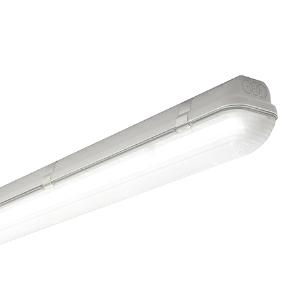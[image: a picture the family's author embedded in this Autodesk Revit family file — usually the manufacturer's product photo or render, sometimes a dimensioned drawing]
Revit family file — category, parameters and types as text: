
# Revit family: 3f_filippi_-_3f_linda_soft_3f_filippi_-_58731_-_3f_linda_led_soft_1x12w_l660
name_source: partatom
category: Lighting Fixtures
units: mm (PartAtom-declared; Revit-internal decimal feet)

## family parameters
Cut with Voids When Loaded = No
Host = Face
Light Source = No
Part Type = Normal
Room Calculation Point = No
Round Connector Dimension = Use Diameter
Shared = No

## types (1)
- 3F Filippi - 3F Linda Soft (1 x LED, 1866 lm, 14 W, 4000 K)
    Apparent Load = 14 VA
    Approval mark = CE
    CIE Flux Codes = 39 68 88 89 100
    Color Rendering = 80
    Color Temperature = 4000 K
    Control Gear = Electronic ballast
    Default Elevation = 1800 mm
    Description = ILLUMINOTECHNICAL
Luminous efficiency 100% (DLOR 89%, ULOR 11%).
Initial luminous flux of the luminaire 1866 lm.
Direct symmetric distribution.
Installation Interdistance Transv.D = 1.39 x hu - Long.D = 1.21 x hu.
Tabular UGR (CIE 117 - 4H-8H; S=0.25H; 70/50/20): RUG 23.7 - 20.5.
Beam angle: 149° - 108°.
Luminous efficacy 133 lm/W.
Lifetime (L93/B10): 30000 h. (tq+25°C)
Lifetime (L90/B10): 50000 h. (tq+25°C)
Lifetime (L85/B10): 80000 h. (tq+25°C)
Lifetime (L80/B10): 100000 h. (tq+25°C)
Lifetime (L85/B10): 50000 h. (tq+35°C)
Sudden decreased luminous flux after 50000 hours: 0% (C0).
Photobiological safety in compliance with IEC/TR 62778: RG0 risk exempt, (IEC 62471).
In compliance with IEC/EN 62722-2-1 - IEC/EN 62717 standards.

SOURCE
Linear LED module 12W/840.
Energy efficiency class (UE 2019/2020 - UE 2019/2015): D.
CIE 13.3 Colour rendering index: CRI >80 (R9 <50%).
IES TM-30 Fidelity Index: Rf = 84 Rg = 95.
CCT nominal colour temperature 4000 K.
Colour initial tolerance (MacAdam): SDCM 3.

MECHANICAL
Self-extinguishing V2 polycarbonate housing, injection moulded, RAL 7035 grey.
Ecologic anti-aging injected sealing gasket.
Soft opal diffuser in self-extinguishing V2 polycarbonate, photo-engraved interior, UV stabilised, injection moulded.
Gear-holder reflector in hot-dip galvanised steel, painted with white polyester base.
Snug fit safety snap-lock clips for diffuser mounting in stainless steel, screwdriver opening.
Fixing brackets in stainless steel.
Possibility for technicians to access the interior of the luminaire.
Luminaire with limited surface temperature. - D - (EN 60598-2-24)
Dimensions: 660x100 mm, height 100 mm. Weight 1.2 kg.
IP66 protection degree.
Mechanical strength to impacts IK10 (20 joule).
Glow-wire test resistance 850°C.

ELECTRICAL
Halogen Free electronic wiring 230V-50/60Hz, power factor 0.95, THD <25%, constant output current, SELV, class I, 1 driver.
Power of the luminaire 14 W.
ENEC - CE.
SAFE FLICKER: PstLM=<1 and SVM=<0.4 (IEC TR 61547-1 and IEC TR 63158), to ensure a more comfortable and safe light.
Luminaire compliant with EN 60598-2-22 for power supply from a centralised emergency system CPSS (Central Power Supply System), not incorporated in the luminaire - high risk areas excluded. The default power and flux are 100% in AC and 100% in DC.
Ambient temperature from -20°C to +35°C.
Temperature class T6 max 85°C.
Relative humidity UR: <85%.

INSTALLATION
Ceiling / Suspended / Wall.
All accessories dedicated to this product are available on the Catalog and on our website www.3F-Filippi.com.

APPLICATIONS
Suitable product for food production plants (HACCP), IFS (Food Version 6), BRC (GSFS Food Version 7).
Dry, dusty indoor environments, subject to occasional water splashes.
Luminaires designed for diffuse direct/indirect lighting suitable to provide optimum visual comfort.
Transit areas, stairwells.
Virtually shatterproof polycarbonate compatibly with the fumes / atmospheres that compromise the elasticity of plastic materials.
Suitable for illumination of public car parks and parking grounds referred to DIN 67528:2018-04.

WARNING
Fixture not suitable for cold stores with an ambient temperature <0°C and/or relative humidity >85%.
Luminaire designed for disposal/recycling at end-of-life.
Replaceable (LED only) light source by a professional. Replaceable control gear by a professional.
    Height = 100 mm  [stored 0.328084 ft]
    Lamp = 1 x LED
    Lamp Light Flux = 1866 lm
    Lamp Power = 14 W
    Lamp count = 1
    Length = 660 mm
    Lifetime = 50000 h
    Luminous efficacy = 133 lm/W
    Manufacturer = 3F Filippi
    ModVariant = No
    Model = 3F Filippi - 58731 - 3F Linda LED Soft 1x12W L660
    Mounting Place = Ceiling
    Mounting Type = Pendant
    Number of Poles = 1
    OnlyDefault = Yes
    Power Factor = 1
    Product Name = 3F Filippi - 3F Linda Soft
    Product group = pendant luminaire
    ProductGroupID = 9
    Protection Class = Protection class I
    Protection Degree = IP 66
    RLX_Detail_Level = 1
    RLX_Emergency_Light_Flux = 0 lm
    RLX_Emergency_Type = 0
    RLX_Emergency_Type_DB = No
    RlxData = <blob elided: 59701 chars, md5=1c063c3f>
    Socket = socket
    Standby Power = 0 W
    System Light Flux = 1866 lm
    System Power = 14 W
    Type Comments = Product without accessories
    Type Image = 3ffilippi_3f_linda_led_soft_1x.jpg
    URL = http://relux.com
    VarID = ---
    Voltage = 0 V
    Weight = 0.00 kg
    Width = 100 mm  [stored 0.328084 ft]

note: [stored X ft] marks values corroborated as IEEE doubles in the binary element streams (Revit-internal decimal feet)

## geometry (parser evidence)
native form markers: Blend x4, Sweep x13
no freeform markers — native parametric forms only
